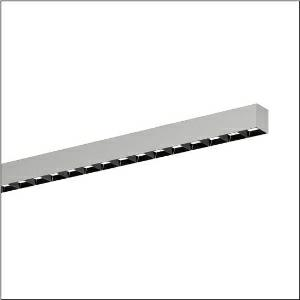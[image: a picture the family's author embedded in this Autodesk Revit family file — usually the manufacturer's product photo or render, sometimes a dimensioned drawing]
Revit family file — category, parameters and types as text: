
# Revit family: silica_21_51mx21dc4asb
name_source: partatom
category: Lighting Fixtures
units: mm (PartAtom-declared; Revit-internal decimal feet)

## family parameters
Cut with Voids When Loaded = No
Host = Face
Light Source = No
Part Type = Normal
Room Calculation Point = No
Round Connector Dimension = Use Diameter
Shared = No

## types (1)
- --- (1 x LED, 10800 lm, 64.8 W, 4000K)
    Apparent Load = 65 VA
    CIE Flux Codes = 87 99 100 100 100
    Color Rendering = 80
    Color Temperature = 4000K
    Default Elevation = 1800 mm
    Description = Silica 21, office luminaire, primary light control with darklight reflector, of PMMA, black, CAT 2 (L<= 3000cd/m²), light emission: direct distribution, primary light characteristic: symmetric, installation type: surface-mounted, LED, rated luminous flux: 10.800lm, luminous efficacy: 167lm/W, light colour: 840, colour temperature: 4000K, control gear: DALI 2, with terminal, 3+2-pole, max. 2.5mm², mains connection: 220..240V, AC, 50/60Hz, rated input power: 64.8W, luminaire housing, of aluminium, metallic grey (RAL 9006), length: 3.004mm, width: 53mm, height: 53mm, protection rating (complete): IP20, insulation class (complete): insulation class I (protective earthing), certification: CE, permissible operating ambient temperature: 0..+35°C, standard: EN 50419, packaging unit: 1 piece
    Height = 53 mm
    Lamp = 1 x LED
    Lamp Light Flux = 10800 lm
    Lamp Power = 64.8 W
    Lamp count = 1
    Length = 3004 mm
    Luminous efficacy = 167 lm/W
    Manufacturer = Siteco
    ModVariant = No
    Model = 51MX21DC4ASB
    Mounting Place = Ceiling
    Mounting Type = Surface mounted
    Number of Poles = 1
    OnlyDefault = Yes
    Power Factor = 1
    Product Name = Silica 21
    Product group = office luminaire | ceiling mounted
    ProductGroupID = 301
    Protection Class = Protection class I
    Protection Degree = IP 20
    RLX_Detail_Level = 1
    RLX_Emergency_Light_Flux = 0 lm
    RLX_Emergency_Type = 0
    RLX_Emergency_Type_DB = No
    RlxData = <blob elided: 62653 chars, md5=5b70f4cc>
    Socket = socket
    Standby Power = 0 W
    System Light Flux = 10800 lm
    System Power = 65 W
    Type Comments = factory setting: luminous flux: 100 % | dim-lin: 254 | 367 mA
    Type Image = l_1335929.jpg
    URL = http://relux.com
    VarID = @adj_123705
    Voltage = 0 V
    Weight = 0.00 kg
    Width = 53 mm

## geometry (parser evidence)
native form markers: Blend x4, Sweep x11
no freeform markers — native parametric forms only
